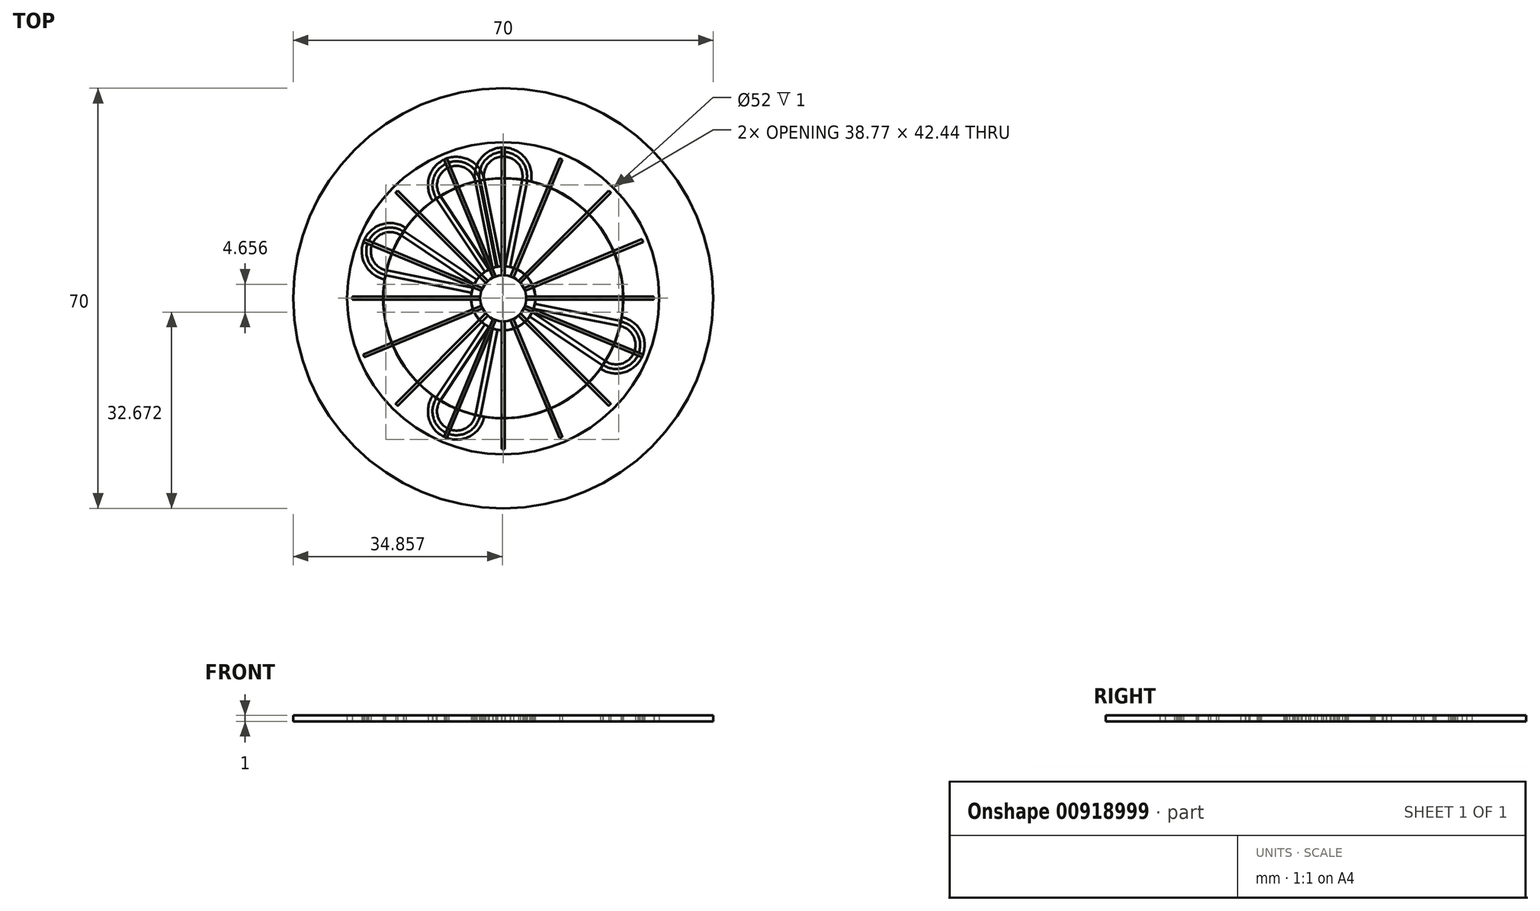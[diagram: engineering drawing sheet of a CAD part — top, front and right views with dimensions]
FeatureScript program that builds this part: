
annotation { "Feature Type Name" : "Feature", "Feature Type Description" : "" }
export const myFeature = defineFeature(function(context is Context, id is Id, definition is map)
    precondition{}
    {
        {
            var Q0;
            Q0=qCreatedBy(makeId("Top.planeOp"),FACE);
            var sketch = newSketch(context, id + "F0", { "sketchPlane" : qUnion([Q0])});
            skCircle(sketch, "E0", {"center": v(0, 0) * mm, "radius": 20 * mm});
            skLineSegment(sketch, "E1", {"start": v(0, 3.84) * mm, "end": v(0, 25.12) * mm});
            skLineSegment(sketch, "E2", {"start": v(-1.04, 5.24) * mm, "end": v(-3.9, 19.62) * mm});
            skLineSegment(sketch, "E3.trimOffspring", {"start": v(-0.3, 5.34) * mm, "end": v(-3.16, 19.75) * mm});
            skCircle(sketch, "E4", {"center": v(0, 0) * mm, "radius": 3.84 * mm});
            skCircle(sketch, "E5.0", {"center": v(0, 0) * mm, "radius": 5.34 * mm});
            skLineSegment(sketch, "E6.trimOffspring", {"start": v(1.04, 5.24) * mm, "end": v(3.9, 19.62) * mm});
            skArc(sketch, "E7", {"start": v(-3.9, 19.62) * mm, "mid": v(0, 24.37) * mm, "end": v(3.9, 19.62) * mm});
            skLineSegment(sketch, "E8.0", {"start": v(0.3, 5.34) * mm, "end": v(3.16, 19.75) * mm});
            skArc(sketch, "E9.0", {"start": v(-4.63, 19.46) * mm, "mid": v(0, 25.12) * mm, "end": v(4.63, 19.46) * mm});
            skArc(sketch, "E10", {"start": v(-3.16, 19.75) * mm, "mid": v(0, 23.6) * mm, "end": v(3.16, 19.75) * mm});
            skLineSegment(sketch, "E11.0", {"start": v(-1.14, 5.22) * mm, "end": v(-4, 19.6) * mm});
            skLineSegment(sketch, "E12.0", {"start": v(1.14, 5.22) * mm, "end": v(4, 19.6) * mm});
            skCircle(sketch, "E13", {"center": v(0, 0) * mm, "radius": 26 * mm});
            skPoint(sketch, "E14.orphan", {"position": v(0, 20) * mm});
            skLineSegment(sketch, "E15.0", {"start": v(0.25, 3.84) * mm, "end": v(0.25, 25.11) * mm});
            skLineSegment(sketch, "E16.0", {"start": v(-0.25, 3.84) * mm, "end": v(-0.25, 25.11) * mm});
            skSolve(sketch);
        }
        {
            var Q0;
            {var subQ0=sQuery(id+"F0.wireOp",EDGE,"E6.trimOffspring");Q0=makeQuery(id+"F0.imprint","IMPRINT",FACE,{"disambiguationData":[TD([[makeQuery(id+"F0.imprint","IMPRINT",EDGE,{"derivedFrom":subQ0}),1.0]])]});}
            var Q1;
            {var subQ0=sQuery(id+"F0.wireOp",EDGE,"E4");var subQ1=sQuery(id+"F0.wireOp",EDGE,"E1");var subQ2=makeQuery(id+"F0.imprint","INTERSECT",VERTEX,{"derivedFrom":[subQ1,subQ0]});Q1=makeQuery(id+"F0.imprint","IMPRINT",FACE,{"disambiguationData":[TD([[makeQuery(id+"F0.imprint","IMPRINT",EDGE,{"disambiguationData":[TD([[subQ2,-1.0]])],"derivedFrom":subQ1}),-1.0]])]});}
            var Q2;
            {var subQ0=sQuery(id+"F0.wireOp",EDGE,"E4");var subQ1=sQuery(id+"F0.wireOp",EDGE,"E1");var subQ2=makeQuery(id+"F0.imprint","INTERSECT",VERTEX,{"derivedFrom":[subQ1,subQ0]});Q2=makeQuery(id+"F0.imprint","IMPRINT",FACE,{"disambiguationData":[TD([[makeQuery(id+"F0.imprint","IMPRINT",EDGE,{"disambiguationData":[TD([[subQ2,-1.0]])],"derivedFrom":subQ1}),1.0]])]});}
            var Q3;
            {var subQ0=sQuery(id+"F0.wireOp",EDGE,"E2");Q3=makeQuery(id+"F0.imprint","IMPRINT",FACE,{"disambiguationData":[TD([[makeQuery(id+"F0.imprint","IMPRINT",EDGE,{"derivedFrom":subQ0}),-1.0]])]});}
            var Q4;
            {var subQ0=sQuery(id+"F0.wireOp",EDGE,"E7");var subQ5=sQuery(id+"F0.wireOp",EDGE,"E15.0");var subQ6=makeQuery(id+"F0.imprint","INTERSECT",VERTEX,{"derivedFrom":[subQ0,subQ5]});Q4=makeQuery(id+"F0.imprint","IMPRINT",FACE,{"disambiguationData":[TD([[makeQuery(id+"F0.imprint","IMPRINT",EDGE,{"disambiguationData":[TD([[subQ6,1.0]])],"derivedFrom":subQ5}),-1.0]])]});}
            var Q5;
            {var subQ0=sQuery(id+"F0.wireOp",EDGE,"E7");var subQ5=sQuery(id+"F0.wireOp",EDGE,"E16.0");var subQ6=makeQuery(id+"F0.imprint","INTERSECT",VERTEX,{"derivedFrom":[subQ0,subQ5]});Q5=makeQuery(id+"F0.imprint","IMPRINT",FACE,{"disambiguationData":[TD([[makeQuery(id+"F0.imprint","IMPRINT",EDGE,{"disambiguationData":[TD([[subQ6,1.0]])],"derivedFrom":subQ5}),1.0]])]});}
            var Q6;
            {var subQ0=sQuery(id+"F0.wireOp",EDGE,"E10");var subQ1=sQuery(id+"F0.wireOp",EDGE,"E1");var subQ2=makeQuery(id+"F0.imprint","INTERSECT",VERTEX,{"derivedFrom":[subQ1,subQ0]});Q6=makeQuery(id+"F0.imprint","IMPRINT",FACE,{"disambiguationData":[TD([[makeQuery(id+"F0.imprint","IMPRINT",EDGE,{"disambiguationData":[TD([[subQ2,-1.0]])],"derivedFrom":subQ1}),1.0]])]});}
            var Q7;
            {var subQ0=sQuery(id+"F0.wireOp",EDGE,"E10");var subQ1=sQuery(id+"F0.wireOp",EDGE,"E1");var subQ2=makeQuery(id+"F0.imprint","INTERSECT",VERTEX,{"derivedFrom":[subQ1,subQ0]});Q7=makeQuery(id+"F0.imprint","IMPRINT",FACE,{"disambiguationData":[TD([[makeQuery(id+"F0.imprint","IMPRINT",EDGE,{"disambiguationData":[TD([[subQ2,-1.0]])],"derivedFrom":subQ1}),-1.0]])]});}
            var Q8;
            {var subQ0=sQuery(id+"F0.wireOp",EDGE,"E2");Q8=makeQuery(id+"F0.imprint","IMPRINT",FACE,{"disambiguationData":[TD([[makeQuery(id+"F0.imprint","IMPRINT",EDGE,{"derivedFrom":subQ0}),1.0]])]});}
            var Q9;
            {var subQ0=sQuery(id+"F0.wireOp",EDGE,"E6.trimOffspring");Q9=makeQuery(id+"F0.imprint","IMPRINT",FACE,{"disambiguationData":[TD([[makeQuery(id+"F0.imprint","IMPRINT",EDGE,{"derivedFrom":subQ0}),-1.0]])]});}
            var Q10;
            {var subQ0=sQuery(id+"F0.wireOp",EDGE,"E9.0");var subQ1=sQuery(id+"F0.wireOp",EDGE,"E1");var subQ2=makeQuery(id+"F0.imprint","INTERSECT",VERTEX,{"derivedFrom":[subQ1,subQ0]});Q10=makeQuery(id+"F0.imprint","IMPRINT",FACE,{"disambiguationData":[TD([[makeQuery(id+"F0.imprint","IMPRINT",EDGE,{"disambiguationData":[TD([[subQ2,1.0]])],"derivedFrom":subQ1}),-1.0]])]});}
            var Q11;
            {var subQ0=sQuery(id+"F0.wireOp",EDGE,"E9.0");var subQ1=sQuery(id+"F0.wireOp",EDGE,"E1");var subQ2=makeQuery(id+"F0.imprint","INTERSECT",VERTEX,{"derivedFrom":[subQ1,subQ0]});Q11=makeQuery(id+"F0.imprint","IMPRINT",FACE,{"disambiguationData":[TD([[makeQuery(id+"F0.imprint","IMPRINT",EDGE,{"disambiguationData":[TD([[subQ2,1.0]])],"derivedFrom":subQ1}),1.0]])]});}
            var Q12;
            {var subQ2=sQuery(id+"F0.wireOp",EDGE,"E15.0");var subQ6=sQuery(id+"F0.wireOp",EDGE,"E4");var subQ7=makeQuery(id+"F0.imprint","INTERSECT",VERTEX,{"derivedFrom":[subQ6,subQ2]});Q12=makeQuery(id+"F0.imprint","IMPRINT",FACE,{"disambiguationData":[TD([[makeQuery(id+"F0.imprint","IMPRINT",EDGE,{"disambiguationData":[TD([[subQ7,1.0]])],"derivedFrom":subQ6}),-1.0]])]});}
            var Q13;
            {var subQ0=sQuery(id+"F0.wireOp",EDGE,"E9.0");var subQ1=sQuery(id+"F0.wireOp",EDGE,"E0");var subQ2=makeQuery(id+"F0.imprint","INTERSECT",VERTEX,{"disambiguationData":[OD(0.0)],"derivedFrom":[subQ1,subQ0]});Q13=makeQuery(id+"F0.imprint","IMPRINT",FACE,{"disambiguationData":[TD([[makeQuery(id+"F0.imprint","IMPRINT",EDGE,{"disambiguationData":[TD([[subQ2,1.0]])],"derivedFrom":subQ1}),-1.0]])]});}
            var Q14;
            {var subQ0=sQuery(id+"F0.wireOp",EDGE,"E9.0");var subQ1=sQuery(id+"F0.wireOp",EDGE,"E0");var subQ2=makeQuery(id+"F0.imprint","INTERSECT",VERTEX,{"disambiguationData":[OD(1.0)],"derivedFrom":[subQ1,subQ0]});Q14=makeQuery(id+"F0.imprint","IMPRINT",FACE,{"disambiguationData":[TD([[makeQuery(id+"F0.imprint","IMPRINT",EDGE,{"disambiguationData":[TD([[subQ2,-1.0]])],"derivedFrom":subQ1}),-1.0]])]});}
            extrude(context, id + "F1", {"entities" : qUnion([Q0, Q1, Q2, Q3, Q4, Q5, Q6, Q7, Q8, Q9, Q10, Q11, Q12, Q13, Q14]), "depth" : 1 * mm, "offsetDistance" : 25 * mm});
        }
        {
            var Q0;
            Q0=makeQuery(id+"F1.opExtrude","SWEPT_BODY",BODY,{"disambiguationData":[OSD([sQuery(id+"F0.wireOp",EDGE,"E0"),sQuery(id+"F0.wireOp",EDGE,"E2"),sQuery(id+"F0.wireOp",EDGE,"E3.trimOffspring"),sQuery(id+"F0.wireOp",EDGE,"E4"),sQuery(id+"F0.wireOp",EDGE,"E5.0"),sQuery(id+"F0.wireOp",EDGE,"E6.trimOffspring"),sQuery(id+"F0.wireOp",EDGE,"E8.0"),sQuery(id+"F0.wireOp",EDGE,"E9.0"),sQuery(id+"F0.wireOp",EDGE,"E10")])]});
            var Q1;
            Q1=makeQuery(id+"F1.opExtrude","CAP_EDGE",EDGE,{"disambiguationData":[OSD([sQuery(id+"F0.wireOp",EDGE,"E4")])],"isStart":false});
            transform(context, id + "F2", {"entities" : qUnion([Q0]), "transformType" : TransformType.ROTATION, "transformAxis" : qUnion([Q1]), "angle" : 22.5 * degree, "makeCopy" : true});
        }
        {
            var Q0;
            Q0=makeQuery(id+"F2.opPattern","COPY",BODY,{"derivedFrom":makeQuery(id+"F1.opExtrude","SWEPT_BODY",BODY,{"disambiguationData":[OSD([sQuery(id+"F0.wireOp",EDGE,"E0"),sQuery(id+"F0.wireOp",EDGE,"E3.trimOffspring"),sQuery(id+"F0.wireOp",EDGE,"E4"),sQuery(id+"F0.wireOp",EDGE,"E5.0"),sQuery(id+"F0.wireOp",EDGE,"E8.0"),sQuery(id+"F0.wireOp",EDGE,"E9.0"),sQuery(id+"F0.wireOp",EDGE,"E10"),sQuery(id+"F0.wireOp",EDGE,"E11.0"),sQuery(id+"F0.wireOp",EDGE,"E12.0")])]}),"instanceName":"1"});
            var Q1;
            Q1=sQuery(id+"F0.wireOp",EDGE,"E4");
            transform(context, id + "F3", {"entities" : qUnion([Q0]), "transformType" : TransformType.ROTATION, "transformAxis" : qUnion([Q1]), "angle" : 45 * degree, "makeCopy" : true});
        }
        {
            var Q0;
            Q0=makeQuery(id+"F3.opPattern","COPY",BODY,{"derivedFrom":makeQuery(id+"F2.opPattern","COPY",BODY,{"derivedFrom":makeQuery(id+"F1.opExtrude","SWEPT_BODY",BODY,{"disambiguationData":[OSD([sQuery(id+"F0.wireOp",EDGE,"E0"),sQuery(id+"F0.wireOp",EDGE,"E3.trimOffspring"),sQuery(id+"F0.wireOp",EDGE,"E4"),sQuery(id+"F0.wireOp",EDGE,"E5.0"),sQuery(id+"F0.wireOp",EDGE,"E8.0"),sQuery(id+"F0.wireOp",EDGE,"E9.0"),sQuery(id+"F0.wireOp",EDGE,"E10"),sQuery(id+"F0.wireOp",EDGE,"E11.0"),sQuery(id+"F0.wireOp",EDGE,"E12.0"),sQuery(id+"F0.wireOp",EDGE,"E13")])]}),"instanceName":"1"}),"instanceName":"1"});
            var Q1;
            Q1=makeQuery(id+"F3.opPattern","COPY",EDGE,{"derivedFrom":makeQuery(id+"F2.opPattern","COPY",EDGE,{"derivedFrom":makeQuery(id+"F1.opExtrude","CAP_EDGE",EDGE,{"disambiguationData":[OSD([sQuery(id+"F0.wireOp",EDGE,"E4")])],"isStart":false}),"instanceName":"1"}),"instanceName":"1"});
            transform(context, id + "F4", {"entities" : qUnion([Q0]), "transformType" : TransformType.ROTATION, "transformAxis" : qUnion([Q1]), "angle" : 90 * degree, "makeCopy" : true});
        }
        {
            var Q0;
            Q0=makeQuery(id+"F3.opPattern","COPY",BODY,{"derivedFrom":makeQuery(id+"F2.opPattern","COPY",BODY,{"derivedFrom":makeQuery(id+"F1.opExtrude","SWEPT_BODY",BODY,{"disambiguationData":[OSD([sQuery(id+"F0.wireOp",EDGE,"E0"),sQuery(id+"F0.wireOp",EDGE,"E3.trimOffspring"),sQuery(id+"F0.wireOp",EDGE,"E4"),sQuery(id+"F0.wireOp",EDGE,"E5.0"),sQuery(id+"F0.wireOp",EDGE,"E8.0"),sQuery(id+"F0.wireOp",EDGE,"E9.0"),sQuery(id+"F0.wireOp",EDGE,"E10"),sQuery(id+"F0.wireOp",EDGE,"E11.0"),sQuery(id+"F0.wireOp",EDGE,"E12.0"),sQuery(id+"F0.wireOp",EDGE,"E13")])]}),"instanceName":"1"}),"instanceName":"1"});
            var Q1;
            Q1=sQuery(id+"F0.wireOp",EDGE,"E4");
            transform(context, id + "F5", {"entities" : qUnion([Q0]), "transformType" : TransformType.ROTATION, "transformAxis" : qUnion([Q1]), "angle" : 180 * degree, "makeCopy" : true});
        }
        {
            var Q0;
            Q0=qCreatedBy(makeId("Top.planeOp"),FACE);
            var sketch = newSketch(context, id + "F6", { "sketchPlane" : qUnion([Q0])});
            skCircle(sketch, "E17", {"center": v(0, 0) * mm, "radius": 35 * mm});
            skSolve(sketch);
        }
        {
            var Q0;
            Q0=makeQuery(id+"F6.imprint","IMPRINT",FACE,{"disambiguationData":[TD([[makeQuery(id+"F6.imprint","IMPRINT",EDGE,{"derivedFrom":sQuery(id+"F6.wireOp",EDGE,"E17")}),1.0]])]});
            extrude(context, id + "F7", {"entities" : qUnion([Q0]), "depth" : 1 * mm, "offsetDistance" : 25 * mm});
        }
        {
            var Q0;
            Q0=makeQuery(id+"F3.opPattern","COPY",BODY,{"derivedFrom":makeQuery(id+"F2.opPattern","COPY",BODY,{"derivedFrom":makeQuery(id+"F1.opExtrude","SWEPT_BODY",BODY,{"disambiguationData":[OSD([sQuery(id+"F0.wireOp",EDGE,"E0"),sQuery(id+"F0.wireOp",EDGE,"E3.trimOffspring"),sQuery(id+"F0.wireOp",EDGE,"E4"),sQuery(id+"F0.wireOp",EDGE,"E5.0"),sQuery(id+"F0.wireOp",EDGE,"E8.0"),sQuery(id+"F0.wireOp",EDGE,"E9.0"),sQuery(id+"F0.wireOp",EDGE,"E10"),sQuery(id+"F0.wireOp",EDGE,"E11.0"),sQuery(id+"F0.wireOp",EDGE,"E12.0")])]}),"instanceName":"1"}),"instanceName":"1"});
            var Q1;
            Q1=makeQuery(id+"F7.opExtrude","SWEPT_BODY",BODY,{"disambiguationData":[OSD([sQuery(id+"F6.wireOp",EDGE,"E17")])]});
            booleanBodies(context, id + "F8", {"operationType" : BooleanOperationType.SUBTRACTION, "tools" : qUnion([Q0]), "targets" : qUnion([Q1])});
        }
        {
            var Q0;
            {var subQ0=sQuery(id+"F0.wireOp",EDGE,"E9.0");var subQ1=sQuery(id+"F0.wireOp",EDGE,"E1");var subQ2=makeQuery(id+"F0.imprint","INTERSECT",VERTEX,{"derivedFrom":[subQ1,subQ0]});Q0=makeQuery(id+"F0.imprint","IMPRINT",FACE,{"disambiguationData":[TD([[makeQuery(id+"F0.imprint","IMPRINT",EDGE,{"disambiguationData":[TD([[subQ2,1.0]])],"derivedFrom":subQ1}),-1.0]])]});}
            var Q1;
            {var subQ0=sQuery(id+"F0.wireOp",EDGE,"E9.0");var subQ1=sQuery(id+"F0.wireOp",EDGE,"E1");var subQ2=makeQuery(id+"F0.imprint","INTERSECT",VERTEX,{"derivedFrom":[subQ1,subQ0]});Q1=makeQuery(id+"F0.imprint","IMPRINT",FACE,{"disambiguationData":[TD([[makeQuery(id+"F0.imprint","IMPRINT",EDGE,{"disambiguationData":[TD([[subQ2,1.0]])],"derivedFrom":subQ1}),1.0]])]});}
            var Q2;
            {var subQ0=sQuery(id+"F0.wireOp",EDGE,"E10");var subQ1=sQuery(id+"F0.wireOp",EDGE,"E1");var subQ2=makeQuery(id+"F0.imprint","INTERSECT",VERTEX,{"derivedFrom":[subQ1,subQ0]});Q2=makeQuery(id+"F0.imprint","IMPRINT",FACE,{"disambiguationData":[TD([[makeQuery(id+"F0.imprint","IMPRINT",EDGE,{"disambiguationData":[TD([[subQ2,-1.0]])],"derivedFrom":subQ1}),1.0]])]});}
            var Q3;
            {var subQ0=sQuery(id+"F0.wireOp",EDGE,"E10");var subQ1=sQuery(id+"F0.wireOp",EDGE,"E1");var subQ2=makeQuery(id+"F0.imprint","INTERSECT",VERTEX,{"derivedFrom":[subQ1,subQ0]});Q3=makeQuery(id+"F0.imprint","IMPRINT",FACE,{"disambiguationData":[TD([[makeQuery(id+"F0.imprint","IMPRINT",EDGE,{"disambiguationData":[TD([[subQ2,-1.0]])],"derivedFrom":subQ1}),-1.0]])]});}
            var Q4;
            {var subQ0=sQuery(id+"F0.wireOp",EDGE,"E15.0");var subQ1=sQuery(id+"F0.wireOp",EDGE,"E0");var subQ2=makeQuery(id+"F0.imprint","INTERSECT",VERTEX,{"derivedFrom":[subQ1,subQ0]});Q4=makeQuery(id+"F0.imprint","IMPRINT",FACE,{"disambiguationData":[TD([[makeQuery(id+"F0.imprint","IMPRINT",EDGE,{"disambiguationData":[TD([[subQ2,-1.0]])],"derivedFrom":subQ1}),-1.0]])]});}
            var Q5;
            {var subQ0=sQuery(id+"F0.wireOp",EDGE,"E1");var subQ1=sQuery(id+"F0.wireOp",EDGE,"E0");var subQ2=makeQuery(id+"F0.imprint","INTERSECT",VERTEX,{"derivedFrom":[subQ1,subQ0]});Q5=makeQuery(id+"F0.imprint","IMPRINT",FACE,{"disambiguationData":[TD([[makeQuery(id+"F0.imprint","IMPRINT",EDGE,{"disambiguationData":[TD([[subQ2,-1.0]])],"derivedFrom":subQ1}),-1.0]])]});}
            var Q6;
            {var subQ0=sQuery(id+"F0.wireOp",EDGE,"E1");var subQ1=sQuery(id+"F0.wireOp",EDGE,"E0");var subQ2=makeQuery(id+"F0.imprint","INTERSECT",VERTEX,{"derivedFrom":[subQ1,subQ0]});Q6=makeQuery(id+"F0.imprint","IMPRINT",FACE,{"disambiguationData":[TD([[makeQuery(id+"F0.imprint","IMPRINT",EDGE,{"disambiguationData":[TD([[subQ2,-1.0]])],"derivedFrom":subQ1}),1.0]])]});}
            var Q7;
            {var subQ0=sQuery(id+"F0.wireOp",EDGE,"E15.0");var subQ1=sQuery(id+"F0.wireOp",EDGE,"E0");var subQ2=makeQuery(id+"F0.imprint","INTERSECT",VERTEX,{"derivedFrom":[subQ1,subQ0]});Q7=makeQuery(id+"F0.imprint","IMPRINT",FACE,{"disambiguationData":[TD([[makeQuery(id+"F0.imprint","IMPRINT",EDGE,{"disambiguationData":[TD([[subQ2,-1.0]])],"derivedFrom":subQ1}),1.0]])]});}
            var Q8;
            {var subQ0=sQuery(id+"F0.wireOp",EDGE,"E4");var subQ1=sQuery(id+"F0.wireOp",EDGE,"E1");var subQ2=makeQuery(id+"F0.imprint","INTERSECT",VERTEX,{"derivedFrom":[subQ1,subQ0]});Q8=makeQuery(id+"F0.imprint","IMPRINT",FACE,{"disambiguationData":[TD([[makeQuery(id+"F0.imprint","IMPRINT",EDGE,{"disambiguationData":[TD([[subQ2,-1.0]])],"derivedFrom":subQ1}),1.0]])]});}
            var Q9;
            {var subQ0=sQuery(id+"F0.wireOp",EDGE,"E4");var subQ1=sQuery(id+"F0.wireOp",EDGE,"E1");var subQ2=makeQuery(id+"F0.imprint","INTERSECT",VERTEX,{"derivedFrom":[subQ1,subQ0]});Q9=makeQuery(id+"F0.imprint","IMPRINT",FACE,{"disambiguationData":[TD([[makeQuery(id+"F0.imprint","IMPRINT",EDGE,{"disambiguationData":[TD([[subQ2,-1.0]])],"derivedFrom":subQ1}),-1.0]])]});}
            extrude(context, id + "F9", {"entities" : qUnion([Q0, Q1, Q2, Q3, Q4, Q5, Q6, Q7, Q8, Q9]), "depth" : 1 * mm, "offsetDistance" : 25 * mm});
        }
        {
            var Q0;
            Q0=makeQuery(id+"F9.opExtrude","SWEPT_BODY",BODY,{"disambiguationData":[OSD([sQuery(id+"F0.wireOp",EDGE,"E4"),sQuery(id+"F0.wireOp",EDGE,"E9.0"),sQuery(id+"F0.wireOp",EDGE,"E15.0"),sQuery(id+"F0.wireOp",EDGE,"E16.0")])]});
            var Q1;
            Q1=makeQuery(id+"F8.opBoolean","COPY",EDGE,{"derivedFrom":makeQuery(id+"F3.opPattern","COPY",EDGE,{"derivedFrom":makeQuery(id+"F2.opPattern","COPY",EDGE,{"derivedFrom":makeQuery(id+"F1.opExtrude","CAP_EDGE",EDGE,{"disambiguationData":[OSD([sQuery(id+"F0.wireOp",EDGE,"E4")])],"isStart":false}),"instanceName":"1"}),"instanceName":"1"})});
            transform(context, id + "F10", {"entities" : qUnion([Q0]), "transformType" : TransformType.ROTATION, "transformAxis" : qUnion([Q1]), "angle" : 22.5 * degree, "makeCopy" : true});
        }
        {
            var Q0;
            Q0=makeQuery(id+"F10.opPattern","COPY",BODY,{"derivedFrom":makeQuery(id+"F9.opExtrude","SWEPT_BODY",BODY,{"disambiguationData":[OSD([sQuery(id+"F0.wireOp",EDGE,"E4"),sQuery(id+"F0.wireOp",EDGE,"E9.0"),sQuery(id+"F0.wireOp",EDGE,"E15.0"),sQuery(id+"F0.wireOp",EDGE,"E16.0")])]}),"instanceName":"1"});
            var Q1;
            Q1=makeQuery(id+"F8.opBoolean","COPY",EDGE,{"derivedFrom":makeQuery(id+"F3.opPattern","COPY",EDGE,{"derivedFrom":makeQuery(id+"F2.opPattern","COPY",EDGE,{"derivedFrom":makeQuery(id+"F1.opExtrude","CAP_EDGE",EDGE,{"disambiguationData":[OSD([sQuery(id+"F0.wireOp",EDGE,"E4")])],"isStart":false}),"instanceName":"1"}),"instanceName":"1"})});
            transform(context, id + "F11", {"entities" : qUnion([Q0]), "transformType" : TransformType.ROTATION, "transformAxis" : qUnion([Q1]), "angle" : 22.5 * degree, "makeCopy" : true});
        }
        {
            var Q0;
            Q0=makeQuery(id+"F11.opPattern","COPY",BODY,{"derivedFrom":makeQuery(id+"F10.opPattern","COPY",BODY,{"derivedFrom":makeQuery(id+"F9.opExtrude","SWEPT_BODY",BODY,{"disambiguationData":[OSD([sQuery(id+"F0.wireOp",EDGE,"E4"),sQuery(id+"F0.wireOp",EDGE,"E9.0"),sQuery(id+"F0.wireOp",EDGE,"E15.0"),sQuery(id+"F0.wireOp",EDGE,"E16.0")])]}),"instanceName":"1"}),"instanceName":"1"});
            var Q1;
            Q1=makeQuery(id+"F8.opBoolean","COPY",EDGE,{"derivedFrom":makeQuery(id+"F3.opPattern","COPY",EDGE,{"derivedFrom":makeQuery(id+"F2.opPattern","COPY",EDGE,{"derivedFrom":makeQuery(id+"F1.opExtrude","CAP_EDGE",EDGE,{"disambiguationData":[OSD([sQuery(id+"F0.wireOp",EDGE,"E4")])],"isStart":false}),"instanceName":"1"}),"instanceName":"1"})});
            transform(context, id + "F12", {"entities" : qUnion([Q0]), "transformType" : TransformType.ROTATION, "transformAxis" : qUnion([Q1]), "angle" : 22.5 * degree, "makeCopy" : true});
        }
        {
            var Q0;
            Q0=makeQuery(id+"F12.opPattern","COPY",BODY,{"derivedFrom":makeQuery(id+"F11.opPattern","COPY",BODY,{"derivedFrom":makeQuery(id+"F10.opPattern","COPY",BODY,{"derivedFrom":makeQuery(id+"F9.opExtrude","SWEPT_BODY",BODY,{"disambiguationData":[OSD([sQuery(id+"F0.wireOp",EDGE,"E4"),sQuery(id+"F0.wireOp",EDGE,"E9.0"),sQuery(id+"F0.wireOp",EDGE,"E15.0"),sQuery(id+"F0.wireOp",EDGE,"E16.0")])]}),"instanceName":"1"}),"instanceName":"1"}),"instanceName":"1"});
            var Q1;
            Q1=makeQuery(id+"F8.opBoolean","COPY",EDGE,{"derivedFrom":makeQuery(id+"F3.opPattern","COPY",EDGE,{"derivedFrom":makeQuery(id+"F2.opPattern","COPY",EDGE,{"derivedFrom":makeQuery(id+"F1.opExtrude","CAP_EDGE",EDGE,{"disambiguationData":[OSD([sQuery(id+"F0.wireOp",EDGE,"E4")])],"isStart":false}),"instanceName":"1"}),"instanceName":"1"})});
            transform(context, id + "F13", {"entities" : qUnion([Q0]), "transformType" : TransformType.ROTATION, "transformAxis" : qUnion([Q1]), "angle" : 22.5 * degree, "makeCopy" : true});
        }
        {
            var Q0;
            Q0=makeQuery(id+"F13.opPattern","COPY",BODY,{"derivedFrom":makeQuery(id+"F12.opPattern","COPY",BODY,{"derivedFrom":makeQuery(id+"F11.opPattern","COPY",BODY,{"derivedFrom":makeQuery(id+"F10.opPattern","COPY",BODY,{"derivedFrom":makeQuery(id+"F9.opExtrude","SWEPT_BODY",BODY,{"disambiguationData":[OSD([sQuery(id+"F0.wireOp",EDGE,"E4"),sQuery(id+"F0.wireOp",EDGE,"E9.0"),sQuery(id+"F0.wireOp",EDGE,"E15.0"),sQuery(id+"F0.wireOp",EDGE,"E16.0")])]}),"instanceName":"1"}),"instanceName":"1"}),"instanceName":"1"}),"instanceName":"1"});
            var Q1;
            Q1=makeQuery(id+"F12.opPattern","COPY",BODY,{"derivedFrom":makeQuery(id+"F11.opPattern","COPY",BODY,{"derivedFrom":makeQuery(id+"F10.opPattern","COPY",BODY,{"derivedFrom":makeQuery(id+"F9.opExtrude","SWEPT_BODY",BODY,{"disambiguationData":[OSD([sQuery(id+"F0.wireOp",EDGE,"E4"),sQuery(id+"F0.wireOp",EDGE,"E9.0"),sQuery(id+"F0.wireOp",EDGE,"E15.0"),sQuery(id+"F0.wireOp",EDGE,"E16.0")])]}),"instanceName":"1"}),"instanceName":"1"}),"instanceName":"1"});
            var Q2;
            Q2=makeQuery(id+"F11.opPattern","COPY",BODY,{"derivedFrom":makeQuery(id+"F10.opPattern","COPY",BODY,{"derivedFrom":makeQuery(id+"F9.opExtrude","SWEPT_BODY",BODY,{"disambiguationData":[OSD([sQuery(id+"F0.wireOp",EDGE,"E4"),sQuery(id+"F0.wireOp",EDGE,"E9.0"),sQuery(id+"F0.wireOp",EDGE,"E15.0"),sQuery(id+"F0.wireOp",EDGE,"E16.0")])]}),"instanceName":"1"}),"instanceName":"1"});
            var Q3;
            Q3=makeQuery(id+"F10.opPattern","COPY",BODY,{"derivedFrom":makeQuery(id+"F9.opExtrude","SWEPT_BODY",BODY,{"disambiguationData":[OSD([sQuery(id+"F0.wireOp",EDGE,"E4"),sQuery(id+"F0.wireOp",EDGE,"E9.0"),sQuery(id+"F0.wireOp",EDGE,"E15.0"),sQuery(id+"F0.wireOp",EDGE,"E16.0")])]}),"instanceName":"1"});
            var Q4;
            Q4=makeQuery(id+"F9.opExtrude","SWEPT_BODY",BODY,{"disambiguationData":[OSD([sQuery(id+"F0.wireOp",EDGE,"E4"),sQuery(id+"F0.wireOp",EDGE,"E9.0"),sQuery(id+"F0.wireOp",EDGE,"E15.0"),sQuery(id+"F0.wireOp",EDGE,"E16.0")])]});
            var Q5;
            Q5=qCreatedBy(makeId("Right.planeOp"),FACE);
            mirror(context, id + "F14", {"entities" : qUnion([Q0, Q1, Q2, Q3, Q4]), "mirrorPlane" : qUnion([Q5])});
        }
        {
            var Q0;
            Q0=makeQuery(id+"F14.opPattern","COPY",BODY,{"derivedFrom":makeQuery(id+"F13.opPattern","COPY",BODY,{"derivedFrom":makeQuery(id+"F12.opPattern","COPY",BODY,{"derivedFrom":makeQuery(id+"F11.opPattern","COPY",BODY,{"derivedFrom":makeQuery(id+"F10.opPattern","COPY",BODY,{"derivedFrom":makeQuery(id+"F9.opExtrude","SWEPT_BODY",BODY,{"disambiguationData":[OSD([sQuery(id+"F0.wireOp",EDGE,"E4"),sQuery(id+"F0.wireOp",EDGE,"E9.0"),sQuery(id+"F0.wireOp",EDGE,"E15.0"),sQuery(id+"F0.wireOp",EDGE,"E16.0")])]}),"instanceName":"1"}),"instanceName":"1"}),"instanceName":"1"}),"instanceName":"1"}),"instanceName":"1"});
            var Q1;
            Q1=makeQuery(id+"F14.opPattern","COPY",BODY,{"derivedFrom":makeQuery(id+"F12.opPattern","COPY",BODY,{"derivedFrom":makeQuery(id+"F11.opPattern","COPY",BODY,{"derivedFrom":makeQuery(id+"F10.opPattern","COPY",BODY,{"derivedFrom":makeQuery(id+"F9.opExtrude","SWEPT_BODY",BODY,{"disambiguationData":[OSD([sQuery(id+"F0.wireOp",EDGE,"E4"),sQuery(id+"F0.wireOp",EDGE,"E9.0"),sQuery(id+"F0.wireOp",EDGE,"E15.0"),sQuery(id+"F0.wireOp",EDGE,"E16.0")])]}),"instanceName":"1"}),"instanceName":"1"}),"instanceName":"1"}),"instanceName":"1"});
            var Q2;
            Q2=makeQuery(id+"F14.opPattern","COPY",BODY,{"derivedFrom":makeQuery(id+"F11.opPattern","COPY",BODY,{"derivedFrom":makeQuery(id+"F10.opPattern","COPY",BODY,{"derivedFrom":makeQuery(id+"F9.opExtrude","SWEPT_BODY",BODY,{"disambiguationData":[OSD([sQuery(id+"F0.wireOp",EDGE,"E4"),sQuery(id+"F0.wireOp",EDGE,"E9.0"),sQuery(id+"F0.wireOp",EDGE,"E15.0"),sQuery(id+"F0.wireOp",EDGE,"E16.0")])]}),"instanceName":"1"}),"instanceName":"1"}),"instanceName":"1"});
            var Q3;
            Q3=makeQuery(id+"F14.opPattern","COPY",BODY,{"derivedFrom":makeQuery(id+"F10.opPattern","COPY",BODY,{"derivedFrom":makeQuery(id+"F9.opExtrude","SWEPT_BODY",BODY,{"disambiguationData":[OSD([sQuery(id+"F0.wireOp",EDGE,"E4"),sQuery(id+"F0.wireOp",EDGE,"E9.0"),sQuery(id+"F0.wireOp",EDGE,"E15.0"),sQuery(id+"F0.wireOp",EDGE,"E16.0")])]}),"instanceName":"1"}),"instanceName":"1"});
            var Q4;
            Q4=makeQuery(id+"F14.opPattern","COPY",BODY,{"derivedFrom":makeQuery(id+"F9.opExtrude","SWEPT_BODY",BODY,{"disambiguationData":[OSD([sQuery(id+"F0.wireOp",EDGE,"E4"),sQuery(id+"F0.wireOp",EDGE,"E9.0"),sQuery(id+"F0.wireOp",EDGE,"E15.0"),sQuery(id+"F0.wireOp",EDGE,"E16.0")])]}),"instanceName":"1"});
            var Q5;
            Q5=makeQuery(id+"F13.opPattern","COPY",BODY,{"derivedFrom":makeQuery(id+"F12.opPattern","COPY",BODY,{"derivedFrom":makeQuery(id+"F11.opPattern","COPY",BODY,{"derivedFrom":makeQuery(id+"F10.opPattern","COPY",BODY,{"derivedFrom":makeQuery(id+"F9.opExtrude","SWEPT_BODY",BODY,{"disambiguationData":[OSD([sQuery(id+"F0.wireOp",EDGE,"E4"),sQuery(id+"F0.wireOp",EDGE,"E9.0"),sQuery(id+"F0.wireOp",EDGE,"E15.0"),sQuery(id+"F0.wireOp",EDGE,"E16.0")])]}),"instanceName":"1"}),"instanceName":"1"}),"instanceName":"1"}),"instanceName":"1"});
            var Q6;
            Q6=makeQuery(id+"F12.opPattern","COPY",BODY,{"derivedFrom":makeQuery(id+"F11.opPattern","COPY",BODY,{"derivedFrom":makeQuery(id+"F10.opPattern","COPY",BODY,{"derivedFrom":makeQuery(id+"F9.opExtrude","SWEPT_BODY",BODY,{"disambiguationData":[OSD([sQuery(id+"F0.wireOp",EDGE,"E4"),sQuery(id+"F0.wireOp",EDGE,"E9.0"),sQuery(id+"F0.wireOp",EDGE,"E15.0"),sQuery(id+"F0.wireOp",EDGE,"E16.0")])]}),"instanceName":"1"}),"instanceName":"1"}),"instanceName":"1"});
            var Q7;
            Q7=makeQuery(id+"F11.opPattern","COPY",BODY,{"derivedFrom":makeQuery(id+"F10.opPattern","COPY",BODY,{"derivedFrom":makeQuery(id+"F9.opExtrude","SWEPT_BODY",BODY,{"disambiguationData":[OSD([sQuery(id+"F0.wireOp",EDGE,"E4"),sQuery(id+"F0.wireOp",EDGE,"E9.0"),sQuery(id+"F0.wireOp",EDGE,"E15.0"),sQuery(id+"F0.wireOp",EDGE,"E16.0")])]}),"instanceName":"1"}),"instanceName":"1"});
            var Q8;
            Q8=makeQuery(id+"F10.opPattern","COPY",BODY,{"derivedFrom":makeQuery(id+"F9.opExtrude","SWEPT_BODY",BODY,{"disambiguationData":[OSD([sQuery(id+"F0.wireOp",EDGE,"E4"),sQuery(id+"F0.wireOp",EDGE,"E9.0"),sQuery(id+"F0.wireOp",EDGE,"E15.0"),sQuery(id+"F0.wireOp",EDGE,"E16.0")])]}),"instanceName":"1"});
            var Q9;
            Q9=makeQuery(id+"F9.opExtrude","SWEPT_BODY",BODY,{"disambiguationData":[OSD([sQuery(id+"F0.wireOp",EDGE,"E4"),sQuery(id+"F0.wireOp",EDGE,"E9.0"),sQuery(id+"F0.wireOp",EDGE,"E15.0"),sQuery(id+"F0.wireOp",EDGE,"E16.0")])]});
            var Q10;
            Q10=qCreatedBy(makeId("Front.planeOp"),FACE);
            mirror(context, id + "F15", {"entities" : qUnion([Q0, Q1, Q2, Q3, Q4, Q5, Q6, Q7, Q8, Q9]), "mirrorPlane" : qUnion([Q10])});
        }
    });
